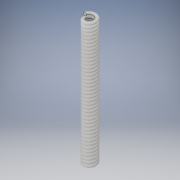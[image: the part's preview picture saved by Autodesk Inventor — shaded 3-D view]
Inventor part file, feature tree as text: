
AUTODESK INVENTOR PART (.ipt)
format: ipt  version: 2018 (Build 220112000, 112)  size: 550,400 bytes
history: native  units: in
note: dims shown in document units (in); Inventor stores cm internally (conversion verified against a paired STEP export)
features: helix x1, sketch x1
ambient origin geometry x8: Origin, YZ Plane, XZ Plane, XY Plane, X Axis, Y Axis, Z Axis, Center Point
bodies: Solid1 (feature_tree)
feature tree (2):
  helix  "Coil1"  [1 undecoded]
  sketch  "Sketch1"  dims[d1=0.044in d2=1.0in d3=0.8268in d4=15.748in d5=0.0in d6=0.0in d7=0.0in d8=0.0in d9=0.0in]
note: 1 required parameter value undecoded (feature->parameter linkage not recoverable at this tier; creation-order binding heuristic only, values carry confidence <= 0.55)
